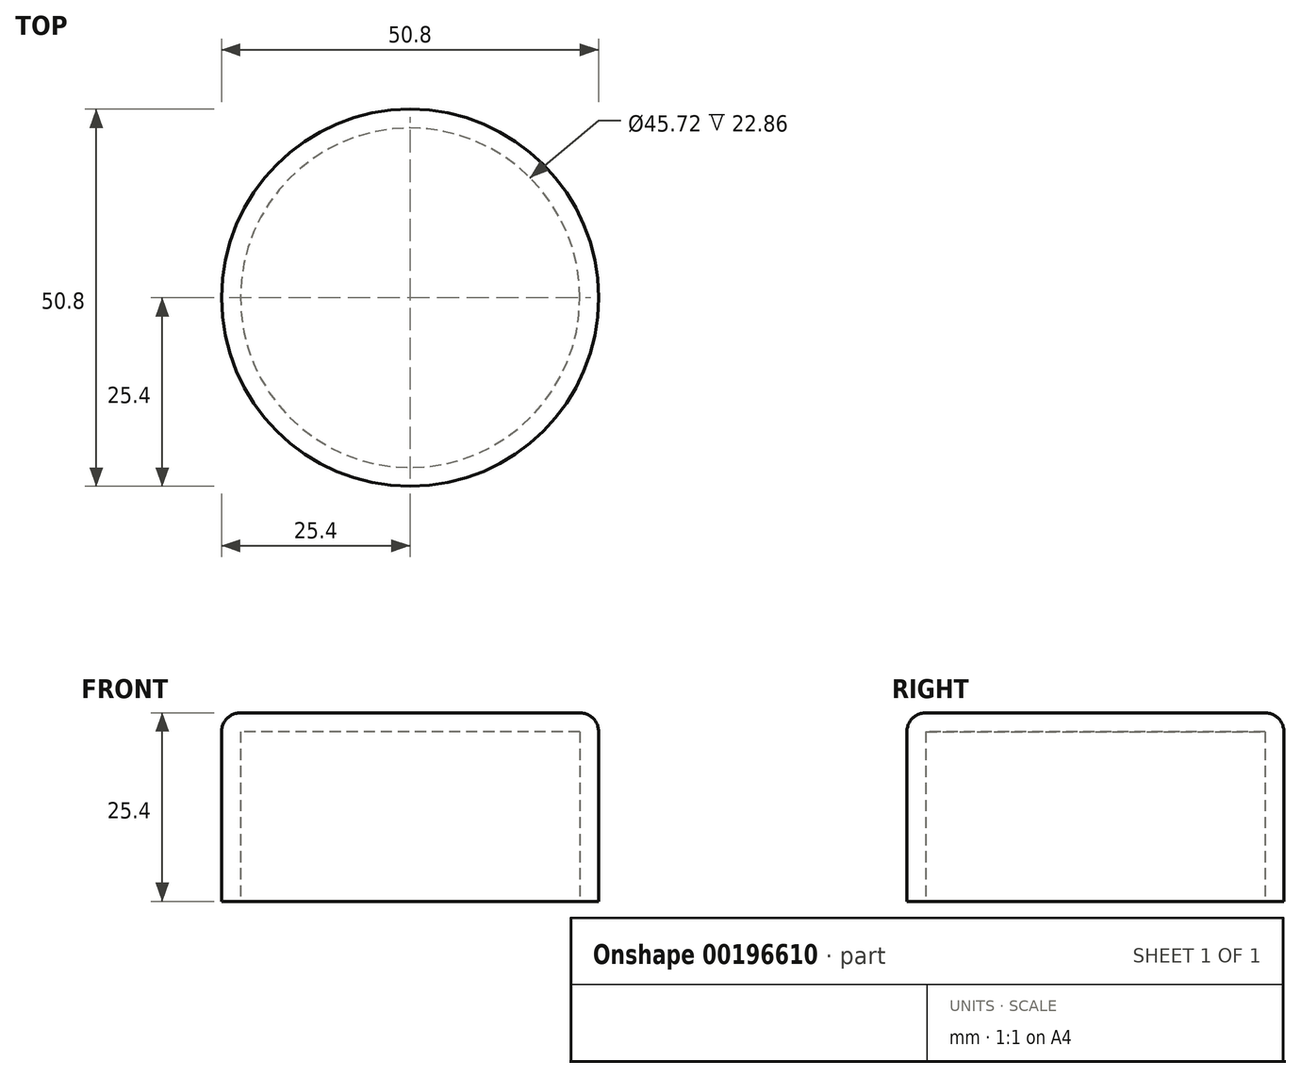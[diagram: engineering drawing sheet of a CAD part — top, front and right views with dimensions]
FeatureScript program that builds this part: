
annotation { "Feature Type Name" : "Feature", "Feature Type Description" : "" }
export const myFeature = defineFeature(function(context is Context, id is Id, definition is map)
    precondition{}
    {
        {
            var Q0;
            Q0=qCreatedBy(makeId("Top.planeOp"),FACE);
            var sketch = newSketch(context, id + "F0", { "sketchPlane" : qUnion([Q0])});
            skCircle(sketch, "E0", {"center": v(0, 0) * mm, "radius": 25.4 * mm});
            skSolve(sketch);
        }
        {
            var Q0;
            Q0=makeQuery(id+"F0.imprint","IMPRINT",FACE,{"disambiguationData":[TD([[makeQuery(id+"F0.imprint","IMPRINT",EDGE,{"derivedFrom":sQuery(id+"F0.wireOp",EDGE,"E0")}),1.0]])]});
            extrude(context, id + "F1", {"entities" : qUnion([Q0]), "endBound" : BoundingType.SYMMETRIC, "depth" : 25.4 * mm});
        }
        {
            var Q0;
            Q0=makeQuery(id+"F1.opExtrude","CAP_FACE",FACE,{"disambiguationData":[OSD([sQuery(id+"F0.wireOp",EDGE,"E0")])],"isStart":true});
            shell(context, id + "F2", {"entities" : qUnion([Q0]), "thickness" : 2.54 * mm});
        }
        {
            var Q0;
            Q0=makeQuery(id+"F1.opExtrude","CAP_EDGE",EDGE,{"disambiguationData":[OSD([sQuery(id+"F0.wireOp",EDGE,"E0")])],"isStart":false});
            fillet(context, id + "F3", {"entities" : qUnion([Q0]), "radius" : 2.54 * mm, "tangentPropagation" : true, "allowEdgeOverflow" : false});
        }
    });
